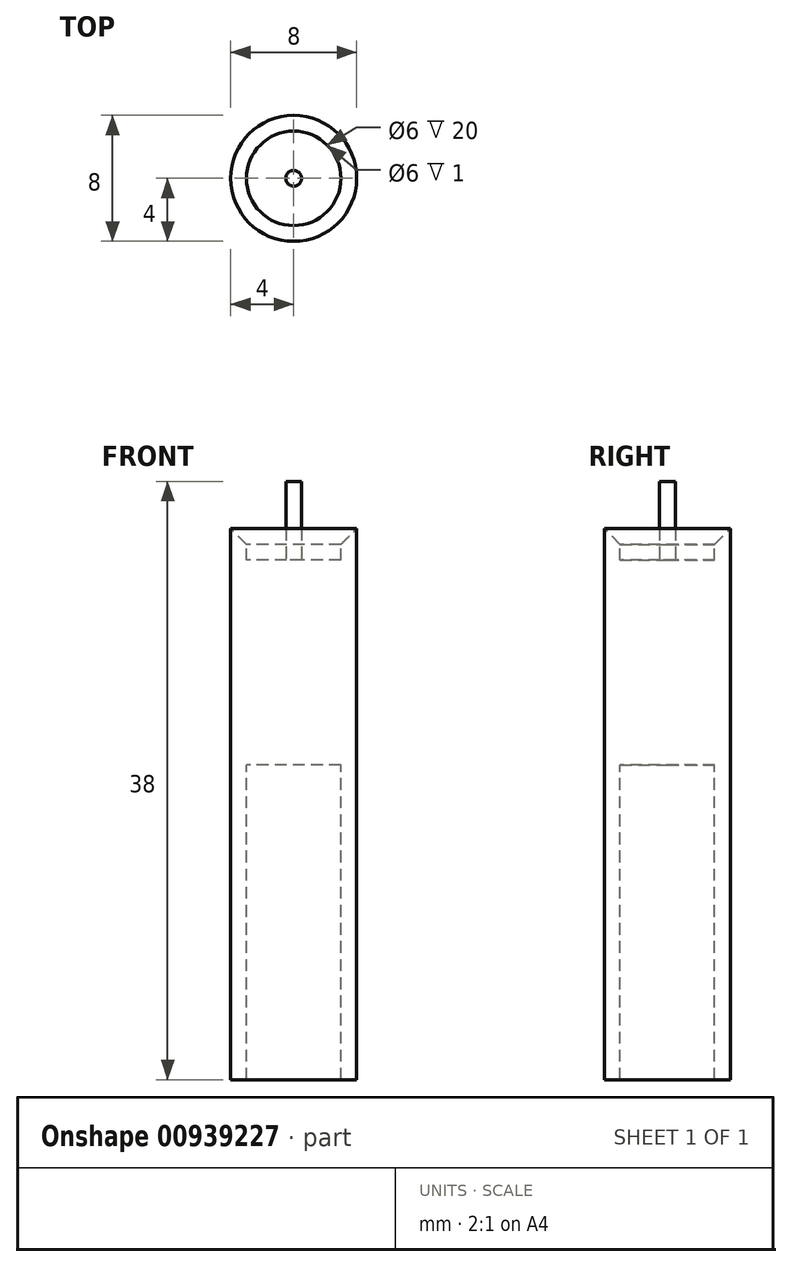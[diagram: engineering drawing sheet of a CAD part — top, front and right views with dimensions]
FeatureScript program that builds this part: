
annotation { "Feature Type Name" : "Feature", "Feature Type Description" : "" }
export const myFeature = defineFeature(function(context is Context, id is Id, definition is map)
    precondition{}
    {
        {
            var Q0;
            Q0=qCreatedBy(makeId("Top.planeOp"),FACE);
            var sketch = newSketch(context, id + "F0", { "sketchPlane" : qUnion([Q0])});
            skCircle(sketch, "E0", {"center": v(0, 0) * mm, "radius": 3 * mm});
            skCircle(sketch, "E1", {"center": v(0, 0) * mm, "radius": 4 * mm});
            skSolve(sketch);
        }
        {
            var Q0;
            Q0=makeQuery(id+"F0.imprint","IMPRINT",FACE,{"disambiguationData":[TD([[makeQuery(id+"F0.imprint","IMPRINT",EDGE,{"derivedFrom":sQuery(id+"F0.wireOp",EDGE,"E0")}),-1.0]])]});
            extrude(context, id + "F1", {"entities" : qUnion([Q0]), "oppositeDirection" : true, "depth" : 20 * mm, "offsetDistance" : 25 * mm});
        }
        {
            var Q0;
            Q0=makeQuery(id+"F0.imprint","IMPRINT",FACE,{"disambiguationData":[TD([[makeQuery(id+"F0.imprint","IMPRINT",EDGE,{"derivedFrom":sQuery(id+"F0.wireOp",EDGE,"E0")}),-1.0]])]});
            extrude(context, id + "F2", {"entities" : qUnion([Q0]), "operationType" : NewBodyOperationType.ADD, "depth" : 15 * mm, "offsetDistance" : 25 * mm});
        }
        {
            var Q0;
            Q0=makeQuery(id+"F0.imprint","IMPRINT",FACE,{"disambiguationData":[TD([[makeQuery(id+"F0.imprint","IMPRINT",EDGE,{"derivedFrom":sQuery(id+"F0.wireOp",EDGE,"E0")}),1.0]])]});
            extrude(context, id + "F3", {"entities" : qUnion([Q0]), "operationType" : NewBodyOperationType.ADD, "depth" : 13 * mm, "offsetDistance" : 25 * mm});
        }
        {
            var Q0;
            Q0=makeQuery(id+"F2.opExtrude","CAP_EDGE",EDGE,{"disambiguationData":[OSD([sQuery(id+"F0.wireOp",EDGE,"E0")])],"isStart":false});
            chamfer(context, id + "F4", {"entities" : qUnion([Q0]), "width" : 1 * mm, "tangentPropagation" : true});
        }
        {
            var Q0;
            Q0=makeQuery(id+"F3.opExtrude","CAP_FACE",FACE,{"disambiguationData":[OSD([sQuery(id+"F0.wireOp",EDGE,"E0")])],"isStart":false});
            var sketch = newSketch(context, id + "F5", { "sketchPlane" : qUnion([Q0])});
            skCircle(sketch, "E2", {"center": v(0, 0) * mm, "radius": 0.5 * mm});
            skSolve(sketch);
        }
        {
            var Q0;
            Q0=makeQuery(id+"F5.imprint","IMPRINT",FACE,{"disambiguationData":[TD([[makeQuery(id+"F5.imprint","IMPRINT",EDGE,{"derivedFrom":sQuery(id+"F5.wireOp",EDGE,"E2")}),1.0]])]});
            extrude(context, id + "F6", {"entities" : qUnion([Q0]), "operationType" : NewBodyOperationType.ADD, "depth" : 5 * mm, "offsetDistance" : 25 * mm});
        }
    });
